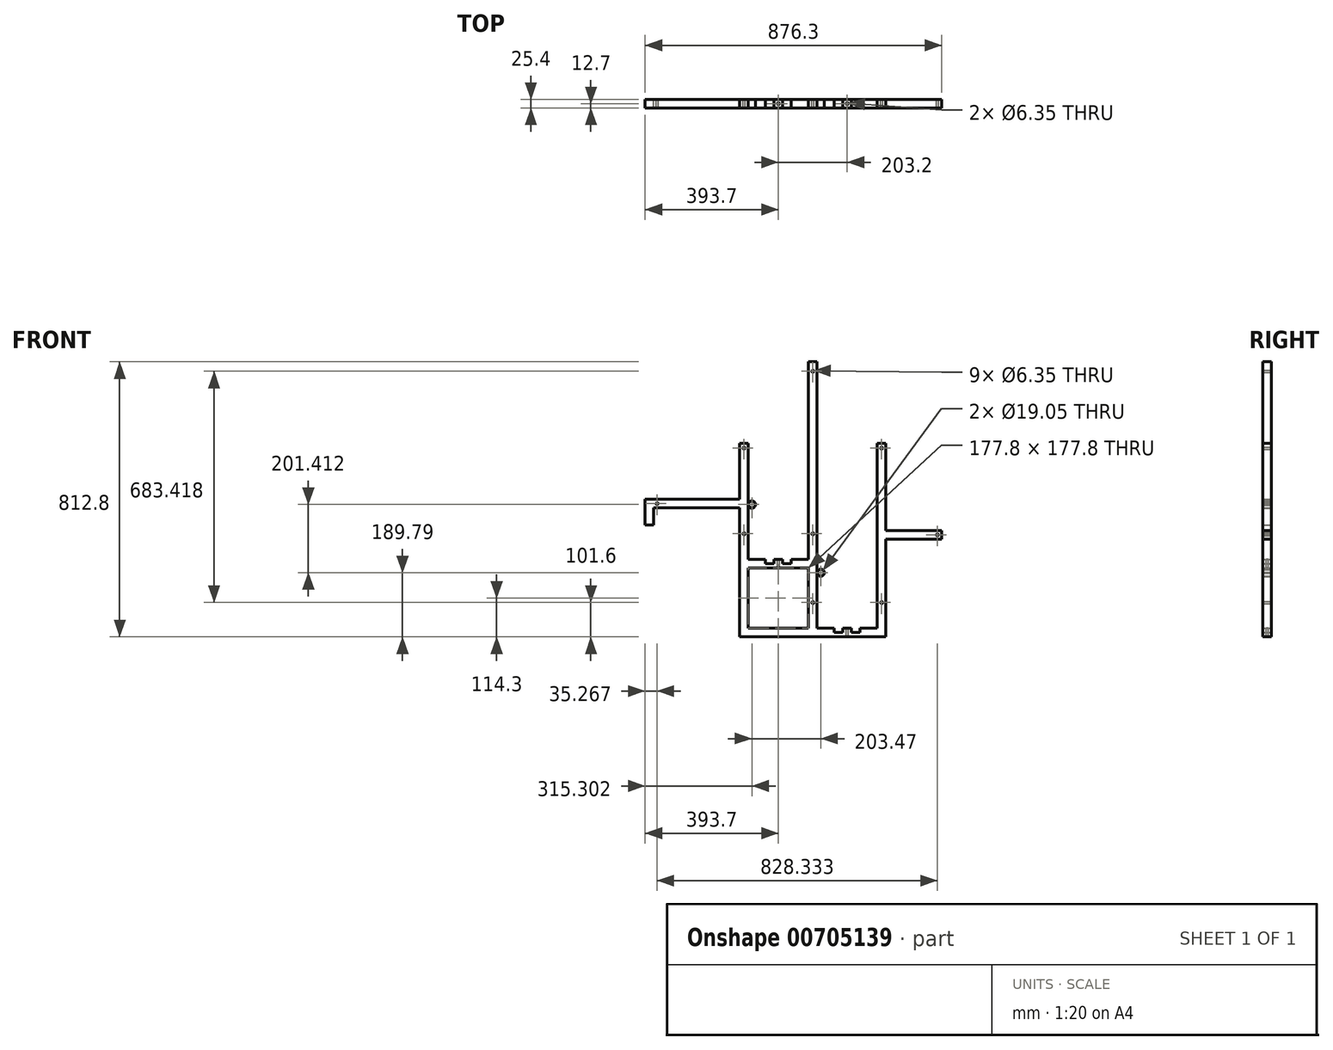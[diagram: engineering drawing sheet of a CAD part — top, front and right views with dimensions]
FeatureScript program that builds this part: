
annotation { "Feature Type Name" : "Feature", "Feature Type Description" : "" }
export const myFeature = defineFeature(function(context is Context, id is Id, definition is map)
    precondition{}
    {
        {
            var Q0;
            Q0=qCreatedBy(makeId("Front.planeOp"),FACE);
            var sketch = newSketch(context, id + "F0", { "sketchPlane" : qUnion([Q0])});
            skLineSegment(sketch, "E0.bottom", {"start": v(127, -12.7) * mm, "end": v(-127, -12.7) * mm});
            skLineSegment(sketch, "E0.top", {"start": v(127, 12.7) * mm, "end": v(-127, 12.7) * mm});
            skLineSegment(sketch, "E0.left", {"start": v(127, -12.7) * mm, "end": v(127, 12.7) * mm});
            skLineSegment(sketch, "E0.right", {"start": v(-127, -12.7) * mm, "end": v(-127, 12.7) * mm});
            skPoint(sketch, "E0.middle", {"position": v(0, 0) * mm});
            skLineSegment(sketch, "E1.bottom", {"start": v(-127, 12.7) * mm, "end": v(-152.4, 12.7) * mm});
            skLineSegment(sketch, "E1.top", {"start": v(-127, -63.5) * mm, "end": v(-152.4, -63.5) * mm});
            skLineSegment(sketch, "E1.left", {"start": v(-127, 12.7) * mm, "end": v(-127, -63.5) * mm});
            skLineSegment(sketch, "E1.right", {"start": v(-152.4, 12.7) * mm, "end": v(-152.4, -63.5) * mm});
            skLineSegment(sketch, "E2.bottom", {"start": v(127, 12.7) * mm, "end": v(152.4, 12.7) * mm});
            skLineSegment(sketch, "E2.top", {"start": v(127, -393.7) * mm, "end": v(152.4, -393.7) * mm});
            skLineSegment(sketch, "E2.left", {"start": v(127, 12.7) * mm, "end": v(127, -393.7) * mm});
            skLineSegment(sketch, "E2.right", {"start": v(152.4, 12.7) * mm, "end": v(152.4, -393.7) * mm});
            skLineSegment(sketch, "E3.bottom", {"start": v(152.4, -393.7) * mm, "end": v(533.4, -393.7) * mm});
            skLineSegment(sketch, "E3.top", {"start": v(152.4, -368.3) * mm, "end": v(406.4, -368.3) * mm});
            skLineSegment(sketch, "E3.left", {"start": v(152.4, -393.7) * mm, "end": v(152.4, -368.3) * mm});
            skLineSegment(sketch, "E3.right", {"start": v(533.4, -393.7) * mm, "end": v(533.4, -368.3) * mm});
            skLineSegment(sketch, "E4.bottom", {"start": v(533.4, -393.7) * mm, "end": v(558.8, -393.7) * mm});
            skLineSegment(sketch, "E4.top", {"start": v(533.4, -190.5) * mm, "end": v(558.8, -190.5) * mm});
            skLineSegment(sketch, "E4.left", {"start": v(533.4, -393.7) * mm, "end": v(533.4, -190.5) * mm});
            skLineSegment(sketch, "E4.right", {"start": v(558.8, -393.7) * mm, "end": v(558.8, -190.5) * mm});
            skLineSegment(sketch, "E5.bottom", {"start": v(330.2, -368.3) * mm, "end": v(355.6, -368.3) * mm});
            skLineSegment(sketch, "E5.top", {"start": v(330.2, 12.7) * mm, "end": v(355.6, 12.7) * mm});
            skLineSegment(sketch, "E5.left", {"start": v(330.2, -368.3) * mm, "end": v(330.2, 12.7) * mm});
            skLineSegment(sketch, "E5.right", {"start": v(355.6, -368.3) * mm, "end": v(355.6, 12.7) * mm});
            skLineSegment(sketch, "E6.bottom", {"start": v(152.4, -165.1) * mm, "end": v(203.2, -165.1) * mm});
            skLineSegment(sketch, "E6.top", {"start": v(152.4, -190.5) * mm, "end": v(330.2, -190.5) * mm});
            skLineSegment(sketch, "E6.left", {"start": v(152.4, -165.1) * mm, "end": v(152.4, -190.5) * mm});
            skLineSegment(sketch, "E6.right", {"start": v(330.2, -165.1) * mm, "end": v(330.2, -190.5) * mm});
            skLineSegment(sketch, "E7.top", {"start": v(203.2, -177.8) * mm, "end": v(228.6, -177.8) * mm});
            skLineSegment(sketch, "E7.left", {"start": v(203.2, -165.1) * mm, "end": v(203.2, -177.8) * mm});
            skLineSegment(sketch, "E7.right", {"start": v(228.6, -165.1) * mm, "end": v(228.6, -177.8) * mm});
            skLineSegment(sketch, "E8.top", {"start": v(279.4, -177.8) * mm, "end": v(254, -177.8) * mm});
            skLineSegment(sketch, "E8.left", {"start": v(279.4, -165.1) * mm, "end": v(279.4, -177.8) * mm});
            skLineSegment(sketch, "E8.right", {"start": v(254, -165.1) * mm, "end": v(254, -177.8) * mm});
            skLineSegment(sketch, "E9.trimOffspring", {"start": v(228.6, -165.1) * mm, "end": v(254, -165.1) * mm});
            skLineSegment(sketch, "E10.trimOffspring", {"start": v(279.4, -165.1) * mm, "end": v(330.2, -165.1) * mm});
            skLineSegment(sketch, "E11.top", {"start": v(406.4, -381) * mm, "end": v(431.8, -381) * mm});
            skLineSegment(sketch, "E11.left", {"start": v(406.4, -368.3) * mm, "end": v(406.4, -381) * mm});
            skLineSegment(sketch, "E11.right", {"start": v(431.8, -368.3) * mm, "end": v(431.8, -381) * mm});
            skLineSegment(sketch, "E12.top", {"start": v(482.6, -381) * mm, "end": v(457.2, -381) * mm});
            skLineSegment(sketch, "E12.left", {"start": v(482.6, -368.3) * mm, "end": v(482.6, -381) * mm});
            skLineSegment(sketch, "E12.right", {"start": v(457.2, -368.3) * mm, "end": v(457.2, -381) * mm});
            skLineSegment(sketch, "E13.trimOffspring", {"start": v(482.6, -368.3) * mm, "end": v(533.4, -368.3) * mm});
            skLineSegment(sketch, "E14.trimOffspring", {"start": v(431.8, -368.3) * mm, "end": v(457.2, -368.3) * mm});
            skCircle(sketch, "E15", {"center": v(546.1, -292.1) * mm, "radius": 3.17 * mm});
            skCircle(sketch, "E16", {"center": v(342.9, -88.9) * mm, "radius": 3.17 * mm});
            skCircle(sketch, "E17", {"center": v(139.7, -88.9) * mm, "radius": 3.17 * mm});
            skCircle(sketch, "E18", {"center": v(162.9, -2.5) * mm, "radius": 10.8 * mm});
            skPoint(sketch, "E18.first.point", {"position": v(152.4, 0) * mm});
            skPoint(sketch, "E18.second.point", {"position": v(173.66, -1.61) * mm});
            skPoint(sketch, "E18.third.point", {"position": v(169.57, -10.98) * mm});
            skCircle(sketch, "E19", {"center": v(162.9, -2.5) * mm, "radius": 9.53 * mm});
            skCircle(sketch, "E20", {"center": v(366.37, -203.9) * mm, "radius": 10.8 * mm});
            skPoint(sketch, "E20.first.point", {"position": v(355.6, -203.2) * mm});
            skPoint(sketch, "E20.second.point", {"position": v(377.04, -202.24) * mm});
            skPoint(sketch, "E20.third.point", {"position": v(366.31, -214.7) * mm});
            skCircle(sketch, "E21", {"center": v(366.37, -203.9) * mm, "radius": 9.53 * mm});
            skCircle(sketch, "E22", {"center": v(342.9, -292.1) * mm, "radius": 3.17 * mm});
            skLineSegment(sketch, "E23.top", {"start": v(127, 177.8) * mm, "end": v(152.4, 177.8) * mm});
            skLineSegment(sketch, "E23.left", {"start": v(127, 12.7) * mm, "end": v(127, 177.8) * mm});
            skLineSegment(sketch, "E23.right", {"start": v(152.4, 12.7) * mm, "end": v(152.4, 177.8) * mm});
            skLineSegment(sketch, "E24.top", {"start": v(330.2, 419.1) * mm, "end": v(355.6, 419.1) * mm});
            skLineSegment(sketch, "E24.left", {"start": v(330.2, 12.7) * mm, "end": v(330.2, 419.1) * mm});
            skLineSegment(sketch, "E24.right", {"start": v(355.6, 12.7) * mm, "end": v(355.6, 419.1) * mm});
            skLineSegment(sketch, "E25.top", {"start": v(533.4, 177.8) * mm, "end": v(558.8, 177.8) * mm});
            skLineSegment(sketch, "E25.left", {"start": v(533.4, -190.5) * mm, "end": v(533.4, 177.8) * mm});
            skLineSegment(sketch, "E25.right", {"start": v(558.8, -190.5) * mm, "end": v(558.8, 177.8) * mm});
            skCircle(sketch, "E26", {"center": v(342.9, 391.32) * mm, "radius": 3.17 * mm});
            skPoint(sketch, "E26.centerSnap0", {"position": v(342.9, 419.1) * mm});
            skLineSegment(sketch, "E27", {"start": v(546.1, 177.8) * mm, "end": v(546.1, 44.1) * mm, "construction": true});
            skLineSegment(sketch, "E28", {"start": v(342.9, 391.32) * mm, "end": v(546.1, 164.13) * mm, "construction": true});
            skLineSegment(sketch, "E29", {"start": v(139.7, 12.7) * mm, "end": v(139.7, 223.98) * mm, "construction": true});
            skLineSegment(sketch, "E30", {"start": v(342.9, 391.32) * mm, "end": v(139.7, 164.13) * mm, "construction": true});
            skLineSegment(sketch, "E31", {"start": v(127, 0) * mm, "end": v(-107.8, 0) * mm, "construction": true});
            skLineSegment(sketch, "E32", {"start": v(139.7, 164.13) * mm, "end": v(-117.13, 0) * mm, "construction": true});
            skLineSegment(sketch, "E33", {"start": v(558.8, -190.5) * mm, "end": v(711.2, -190.5) * mm, "construction": true});
            skLineSegment(sketch, "E34", {"start": v(711.2, -190.5) * mm, "end": v(711.2, 284.14) * mm, "construction": true});
            skLineSegment(sketch, "E35", {"start": v(546.1, 164.13) * mm, "end": v(711.2, -92.08) * mm, "construction": true});
            skLineSegment(sketch, "E36.bottom", {"start": v(723.9, -79.38) * mm, "end": v(558.8, -79.38) * mm});
            skLineSegment(sketch, "E36.top", {"start": v(723.9, -104.78) * mm, "end": v(558.8, -104.78) * mm});
            skLineSegment(sketch, "E36.left", {"start": v(723.9, -79.38) * mm, "end": v(723.9, -104.78) * mm});
            skLineSegment(sketch, "E36.right", {"start": v(558.8, -79.38) * mm, "end": v(558.8, -104.78) * mm});
            skCircle(sketch, "E37", {"center": v(-117.13, 0) * mm, "radius": 3.18 * mm});
            skCircle(sketch, "E38", {"center": v(139.7, 164.13) * mm, "radius": 3.17 * mm});
            skCircle(sketch, "E39", {"center": v(546.1, 164.13) * mm, "radius": 3.17 * mm});
            skCircle(sketch, "E40", {"center": v(711.2, -92.08) * mm, "radius": 3.17 * mm});
            skSolve(sketch);
        }
        {
            var Q0;
            Q0=qSketchRegion(id+"F0",true);
            extrude(context, id + "F1", {"entities" : qUnion([Q0]), "depth" : 25.4 * mm, "offsetDistance" : 25.4 * mm});
        }
        {
            var Q0;
            Q0=makeQuery(id+"F1.opExtrude","SWEPT_FACE",FACE,{"disambiguationData":[OSD([sQuery(id+"F0.wireOp",EDGE,"E9.trimOffspring")])]});
            var sketch = newSketch(context, id + "F2", { "sketchPlane" : qUnion([Q0])});
            skCircle(sketch, "E41", {"center": v(241.3, -12.7) * mm, "radius": 3.17 * mm});
            skPoint(sketch, "E41.centerSnap0", {"position": v(241.3, -25.4) * mm});
            skPoint(sketch, "E41.centerSnap1", {"position": v(254, -12.7) * mm});
            skSolve(sketch);
        }
        {
            var Q0;
            Q0=qSketchRegion(id+"F2",true);
            extrude(context, id + "F3", {"entities" : qUnion([Q0]), "operationType" : NewBodyOperationType.REMOVE, "oppositeDirection" : true, "depth" : 25.4 * mm, "offsetDistance" : 25.4 * mm});
        }
        {
            var Q0;
            Q0=makeQuery(id+"F1.opExtrude","SWEPT_FACE",FACE,{"disambiguationData":[OSD([sQuery(id+"F0.wireOp",EDGE,"E14.trimOffspring")])]});
            var sketch = newSketch(context, id + "F4", { "sketchPlane" : qUnion([Q0])});
            skCircle(sketch, "E42", {"center": v(444.5, -12.7) * mm, "radius": 3.18 * mm});
            skPoint(sketch, "E42.centerSnap0", {"position": v(444.5, -25.4) * mm});
            skPoint(sketch, "E42.centerSnap1", {"position": v(457.2, -12.7) * mm});
            skSolve(sketch);
        }
        {
            var Q0;
            Q0=qSketchRegion(id+"F4",true);
            extrude(context, id + "F5", {"entities" : qUnion([Q0]), "operationType" : NewBodyOperationType.REMOVE, "oppositeDirection" : true, "depth" : 25.4 * mm, "offsetDistance" : 25.4 * mm});
        }
    });
